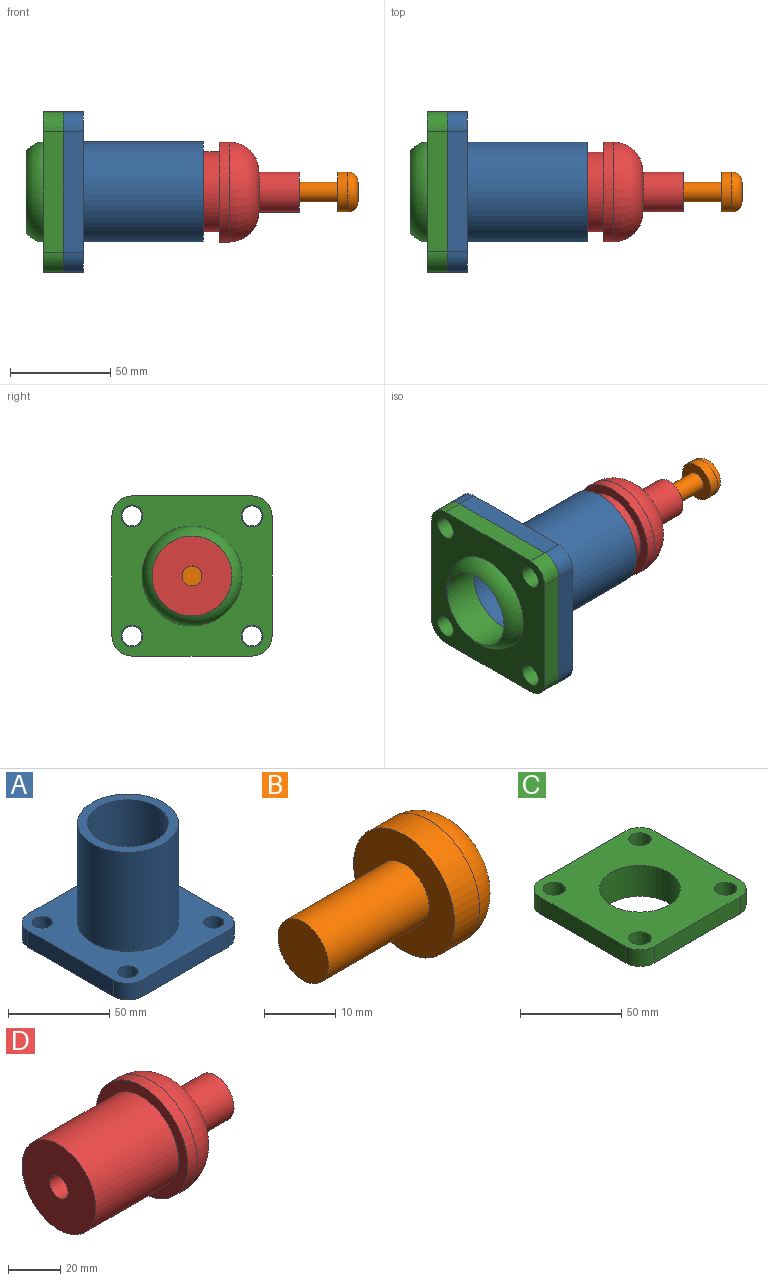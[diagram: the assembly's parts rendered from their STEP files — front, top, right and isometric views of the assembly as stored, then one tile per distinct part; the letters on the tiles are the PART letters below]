
ASSEMBLY  parts=4 mates=5
PART A: 17 faces, bbox 80x80x70 mm
  f0: plane 60x10mm, normal (1,0,0), area 600mm2, adj f1,f11,f12,f13
  f1: cylinder r=10mm len=10mm, axis (0,0,1), area 157.1mm2, adj f0,f2,f12,f13
  f2: plane 60x10mm, normal (0,1,0), area 600mm2, adj f1,f3,f12,f13
  f3: cylinder r=10mm len=10mm, axis (0,0,1), area 157.1mm2, adj f2,f4,f12,f13
  f4: plane 60x10mm, normal (-1,0,0), area 600mm2, adj f3,f5,f12,f13
  f5: cylinder r=10mm len=10mm, axis (0,0,1), area 157.1mm2, adj f4,f6,f12,f13
  f6: plane 60x10mm, normal (0,-1,0), area 600mm2, adj f5,f11,f12,f13
  f7: cylinder r=5mm len=10mm, axis (0,0,1), area 314.2mm2, adj f12,f13
  f8: cylinder r=5mm len=10mm, axis (0,0,1), area 314.2mm2, adj f12,f13
  f9: cylinder r=5mm len=10mm, axis (0,0,1), area 314.2mm2, adj f12,f13
  f10: cylinder r=5mm len=10mm, axis (0,0,1), area 314.2mm2, adj f12,f13
  f11: cylinder r=10mm len=10mm, axis (0,0,1), area 157.1mm2, adj f0,f6,f12,f13
  f12: plane 80x80mm, normal (0,0,-1), area 4743.4mm2, adj f0,f1,f2,f3,f4,f5,f6,f7
  f13: plane 80x80mm, normal (0,0,1), area 4036.5mm2, adj f0,f1,f2,f3,f4,f5,f6,f7
  f14: cylinder r=25mm len=60mm, axis (0,0,-1), area 9424.8mm2, adj f13,f15
  f15: plane 50x50mm, normal (0,0,1), area 706.9mm2, adj f14,f16
  f16: cylinder r=20mm len=70mm, axis (0,0,1), area 8796.5mm2, adj f12,f15
PART B: 6 faces, bbox 30x21.6x21.6 mm
  f0: cylinder r=10mm len=20mm, axis (-1,0,0), area 314.2mm2, adj f1,f5
  f1: plane 20x20mm, normal (-1,0,0), area 235.6mm2, adj f0,f2
  f2: cylinder r=5mm len=20mm, axis (-1,0,0), area 628.3mm2, adj f1,f3
  f3: plane 10x10mm, normal (-1,0,0), area 78.5mm2, adj f2
  f4: plane 10x10mm, normal (1,0,0), area 78.5mm2, adj f5
  f5: torus R=5mm, axis (-1,0,0), area 403.8mm2, adj f0,f4
PART C: 16 faces, bbox 80x80x20 mm
  f0: plane 60x10mm, normal (1,0,0), area 600mm2, adj f1,f11,f12,f13
  f1: cylinder r=10mm len=10mm, axis (0,0,-1), area 157.1mm2, adj f0,f2,f12,f13
  f2: plane 60x10mm, normal (0,1,0), area 600mm2, adj f1,f3,f12,f13
  f3: cylinder r=10mm len=10mm, axis (0,0,-1), area 157.1mm2, adj f2,f4,f12,f13
  f4: plane 60x10mm, normal (-1,0,0), area 600mm2, adj f3,f5,f12,f13
  f5: cylinder r=10mm len=10mm, axis (0,0,-1), area 157.1mm2, adj f4,f6,f12,f13
  f6: plane 60x10mm, normal (0,-1,0), area 600mm2, adj f5,f11,f12,f13
  f7: cylinder r=5.5mm len=11mm, axis (0,0,-1), area 345.6mm2, adj f12,f13
  f8: cylinder r=5.5mm len=11mm, axis (0,0,-1), area 345.6mm2, adj f12,f13
  f9: cylinder r=5.5mm len=11mm, axis (0,0,-1), area 345.6mm2, adj f12,f13
  f10: cylinder r=5.5mm len=11mm, axis (0,0,-1), area 345.6mm2, adj f12,f13
  f11: cylinder r=10mm len=10mm, axis (0,0,-1), area 157.1mm2, adj f0,f6,f12,f13
  f12: plane 80x80mm, normal (0,0,1), area 4677.4mm2, adj f0,f1,f2,f3,f4,f5,f6,f7
  f13: plane 80x80mm, normal (0,0,-1), area 3970.5mm2, adj f0,f1,f2,f3,f4,f5,f6,f7
  f14: torus R=15mm, axis (0,0,-1), area 1531.1mm2, adj f13,f15
  f15: cylinder r=20mm len=40mm, axis (0,0,1), area 2344.9mm2, adj f12,f14
PART D: 8 faces, bbox 85x50x50 mm
  f0: cylinder r=20mm len=45mm, axis (-1,0,0), area 5654.9mm2, adj f1,f2
  f1: plane 40x40mm, normal (-1,0,0), area 1178.1mm2, adj f0,f7
  f2: plane 50x50mm, normal (-1,0,0), area 706.9mm2, adj f0,f6
  f3: plane 20x20mm, normal (1,0,0), area 235.6mm2, adj f4,f7
  f4: cylinder r=10mm len=20mm, axis (-1,0,0), area 1256.6mm2, adj f3,f5
  f5: torus R=10mm, axis (-1,0,0), area 2894.2mm2, adj f4,f6
  f6: cylinder r=25mm len=50mm, axis (-1,0,0), area 785.4mm2, adj f2,f5
  f7: cylinder r=5mm len=85mm, axis (1,0,0), area 2670.4mm2, adj f1,f3
PLACE A rot(axis=(0.71,0,0.71),180deg) t=(-68.49,113.72,-12.2)mm
PLACE B rot(axis=(-1,0,0),76.7deg) t=(38.83,113.72,-12.2)mm
PLACE C rot(axis=(-0.58,0.58,-0.58),120deg) t=(-88.49,113.72,-12.2)mm fixed
PLACE D rot(axis=(-1,0,0),3.4deg) t=(-45.66,113.72,-12.2)mm
MATE cylindrical D.f4 <-> B.f0  axis (1,0,0) through (39.34,113.72,-12.2)mm
MATE cylindrical C.f3 <-> A.f5  axis (-1,0,0) through (-78.49,143.72,-42.2)mm
MATE slider A.f1 <-> C.f9  axis (1,0,0) through (-78.49,83.72,17.8)mm
MATE planar C.f15 <-> A.f16  axis (1,0,0) through (-78.49,113.72,-12.2)mm
MATE cylindrical A.f14 <-> D.f0  axis (1,0,0) through (-8.49,113.72,-12.2)mm
